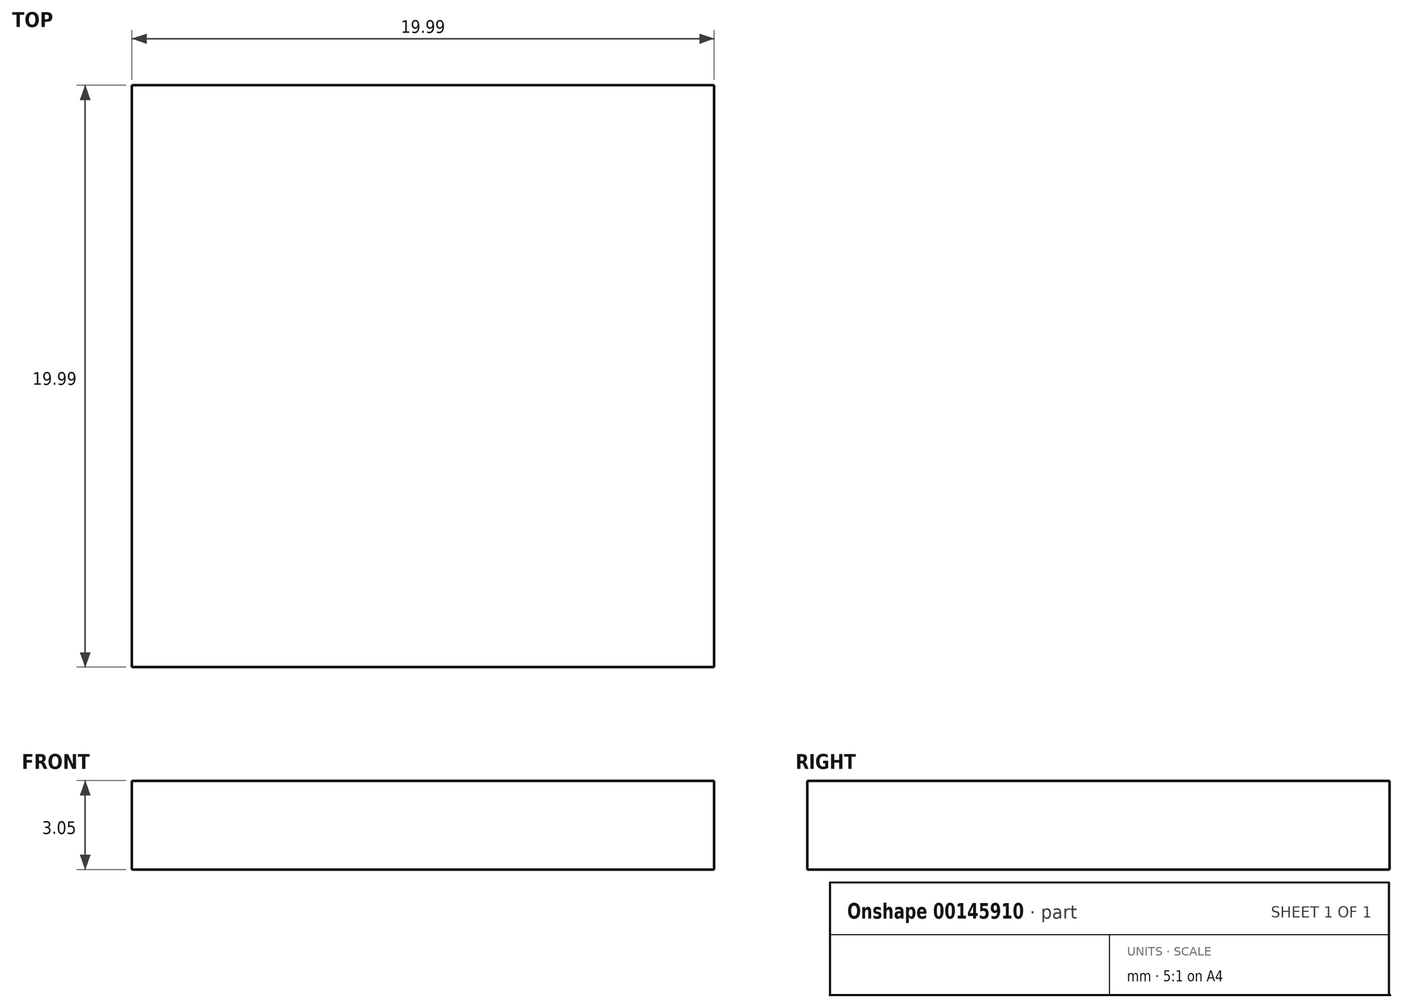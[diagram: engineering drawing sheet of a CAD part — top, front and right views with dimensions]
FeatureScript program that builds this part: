
annotation { "Feature Type Name" : "Feature", "Feature Type Description" : "" }
export const myFeature = defineFeature(function(context is Context, id is Id, definition is map)
    precondition{}
    {
        {
            var Q0;
            Q0=qCreatedBy(makeId("Top.planeOp"),FACE);
            var sketch = newSketch(context, id + "F0", { "sketchPlane" : qUnion([Q0])});
            skLineSegment(sketch, "E0.bottom", {"start": v(0, 0) * mm, "end": v(19.99, 0) * mm});
            skLineSegment(sketch, "E0.top", {"start": v(0, -19.99) * mm, "end": v(19.99, -19.99) * mm});
            skLineSegment(sketch, "E0.left", {"start": v(0, 0) * mm, "end": v(0, -19.99) * mm});
            skLineSegment(sketch, "E0.right", {"start": v(19.99, 0) * mm, "end": v(19.99, -19.99) * mm});
            skSolve(sketch);
        }
        {
            var Q0;
            Q0 = qSketchRegion(id + "F0", true);
            extrude(context, id + "F1", {"entities" : qUnion([Q0]), "depth" : 3.05 * mm});
        }
    });
